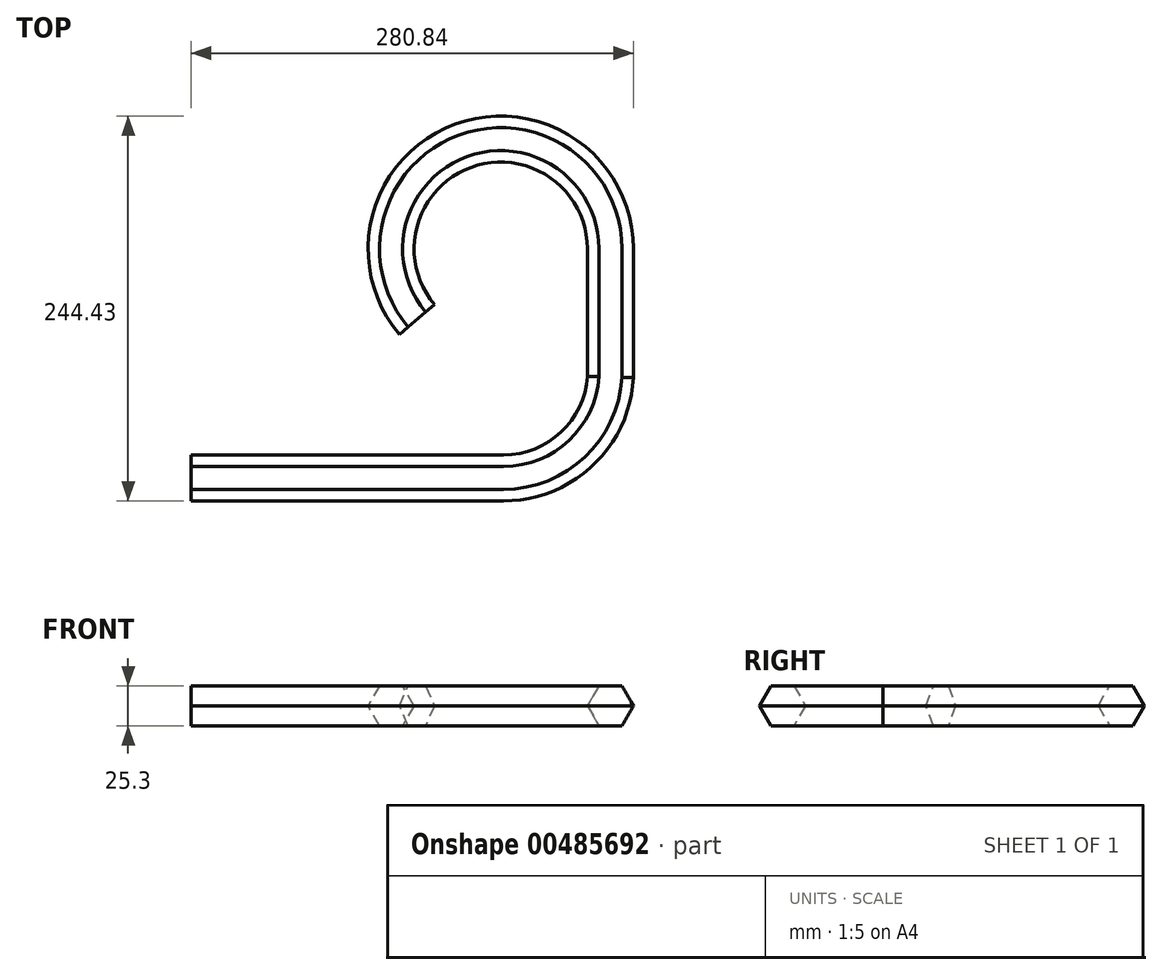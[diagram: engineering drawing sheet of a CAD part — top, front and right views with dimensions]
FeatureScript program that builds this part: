
annotation { "Feature Type Name" : "Feature", "Feature Type Description" : "" }
export const myFeature = defineFeature(function(context is Context, id is Id, definition is map)
    precondition{}
    {
        {
            var Q0;
            Q0=qCreatedBy(makeId("Top.planeOp"),FACE);
            var sketch = newSketch(context, id + "F0", { "sketchPlane" : qUnion([Q0])});
            skLineSegment(sketch, "E0", {"start": v(0, 0) * mm, "end": v(198.38, 0) * mm});
            skArc(sketch, "E1", {"start": v(198.38, 0) * mm, "mid": v(245.06, 18.57) * mm, "end": v(266.23, 64.14) * mm});
            skLineSegment(sketch, "E2", {"start": v(266.23, 64.14) * mm, "end": v(266.23, 145.56) * mm});
            skArc(sketch, "E3", {"start": v(143.37, 100.61) * mm, "mid": v(172.64, 210.97) * mm, "end": v(266.23, 145.56) * mm});
            skSolve(sketch);
        }
        {
            var Q0;
            Q0=qCreatedBy(makeId("Right.planeOp"),FACE);
            var sketch = newSketch(context, id + "F1", { "sketchPlane" : qUnion([Q0])});
            skCircle(sketch, "E4.cCircle", {"center": v(0, 0) * mm, "radius": 12.65 * mm, "construction": true});
            skLineSegment(sketch, "E4.0", {"start": v(7.3, -12.65) * mm, "end": v(-7.3, -12.65) * mm});
            skLineSegment(sketch, "E4.1", {"start": v(-7.3, -12.65) * mm, "end": v(-14.6, 0) * mm});
            skLineSegment(sketch, "E4.2", {"start": v(-14.6, 0) * mm, "end": v(-7.3, 12.65) * mm});
            skLineSegment(sketch, "E4.3", {"start": v(-7.3, 12.65) * mm, "end": v(7.3, 12.65) * mm});
            skLineSegment(sketch, "E4.4", {"start": v(7.3, 12.65) * mm, "end": v(14.6, 0) * mm});
            skLineSegment(sketch, "E4.5", {"start": v(14.6, 0) * mm, "end": v(7.3, -12.65) * mm});
            skPoint(sketch, "E4.0.midPoint", {"position": v(0, -12.65) * mm});
            skSolve(sketch);
        }
        {
            var Q0;
            Q0=makeQuery(id+"F1.imprint","IMPRINT",FACE,{"disambiguationData":[TD([[makeQuery(id+"F1.imprint","IMPRINT",EDGE,{"derivedFrom":sQuery(id+"F1.wireOp",EDGE,"E4.0")}),-1.0]])]});
            var Q1;
            Q1 = qConstructionFilter(qBodyType(qCreatedBy(id + "F0" ,EDGE), BodyType.WIRE), ConstructionObject.NO);
            sweep(context, id + "F2", {"profiles" : qUnion([Q0]), "path" : qUnion([Q1])});
        }
    });
